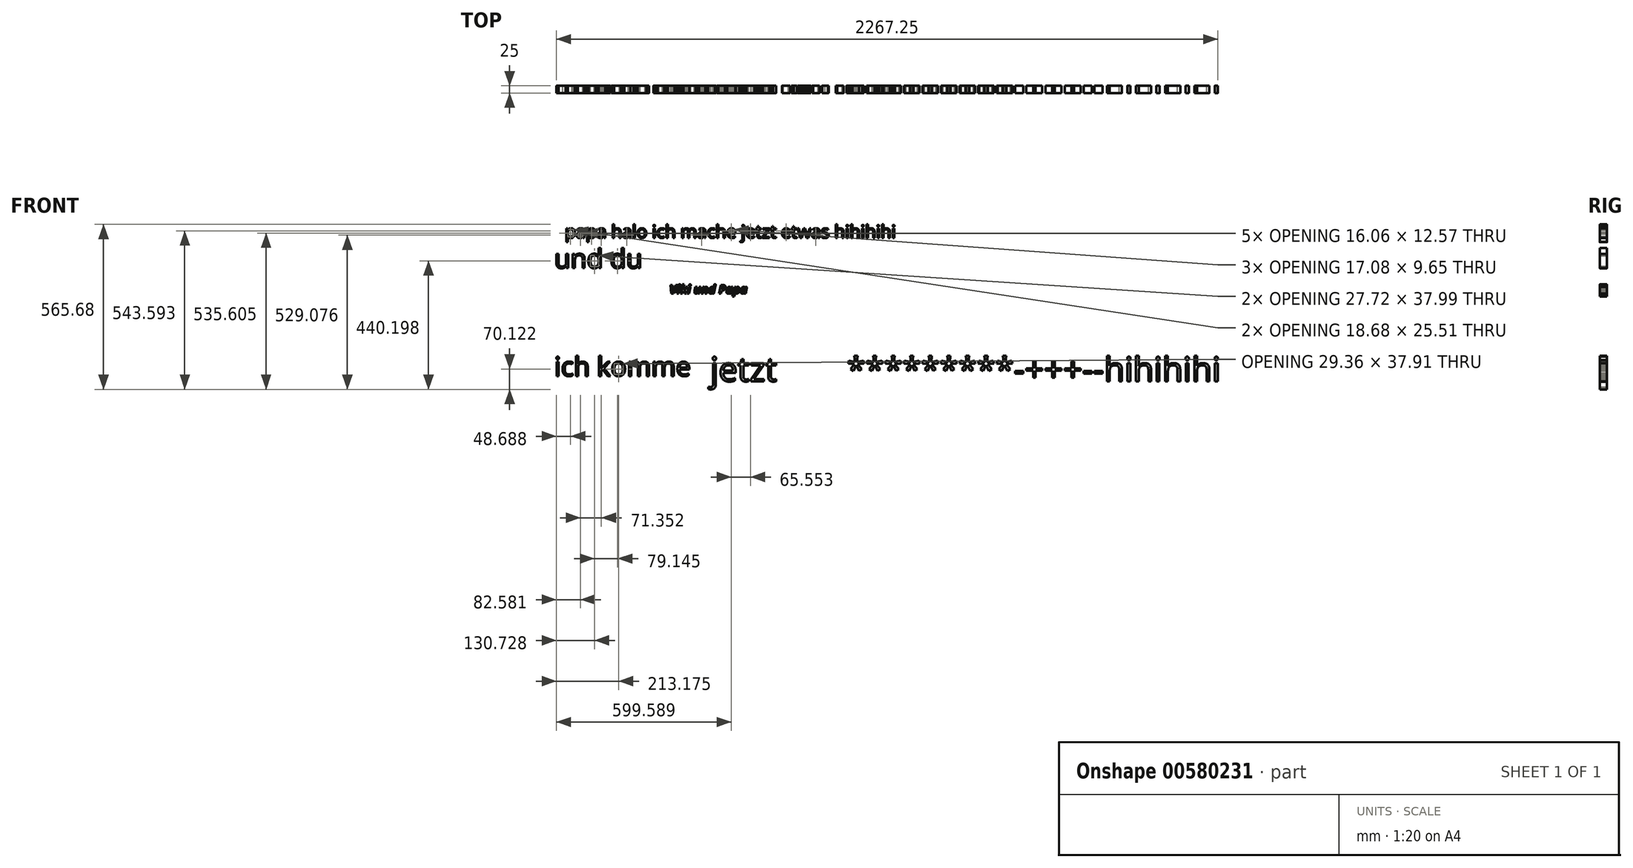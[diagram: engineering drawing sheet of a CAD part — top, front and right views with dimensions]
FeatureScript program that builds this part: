
annotation { "Feature Type Name" : "Feature", "Feature Type Description" : "" }
export const myFeature = defineFeature(function(context is Context, id is Id, definition is map)
    precondition{}
    {
        {
            var Q0;
            Q0=qCreatedBy(makeId("Front.planeOp"),FACE);
            var sketch = newSketch(context, id + "F0", { "sketchPlane" : qUnion([Q0])});
            skText(sketch, "E0", { "text": "papa halo ich mache jetzt etwas hihihihi", "fontName": "OpenSans-Regular.ttf"});
            const initialGuessF0  = {"E0": [-0.0227, 0.032, 1, 0, 0.04395]};
            skSetInitialGuess(sketch, initialGuessF0);
            skSolve(sketch);
        }
        {
            var Q0;
            Q0 = qSketchRegion(id + "F0", true);
            extrude(context, id + "F1", {"entities" : qUnion([Q0]), "depth" : 25 * mm, "offsetDistance" : 25 * mm});
        }
        {
            var Q0;
            Q0=qCreatedBy(makeId("Front.planeOp"),FACE);
            var sketch = newSketch(context, id + "F2", { "sketchPlane" : qUnion([Q0])});
            skText(sketch, "E1", { "text": "und du \n\n\nich komme", "fontName": "OpenSans-Regular.ttf"});
            const initialGuessF2  = {"E1": [-0.05902, -0.07137, 1, 0, 0.0653]};
            skSetInitialGuess(sketch, initialGuessF2);
            skSolve(sketch);
        }
        {
            var Q0;
            Q0 = qSketchRegion(id + "F2", true);
            extrude(context, id + "F3", {"entities" : qUnion([Q0]), "depth" : 25 * mm, "offsetDistance" : 25 * mm});
        }
        {
            var Q0;
            Q0=qCreatedBy(makeId("Front.planeOp"),FACE);
            var sketch = newSketch(context, id + "F4", { "sketchPlane" : qUnion([Q0])});
            skText(sketch, "E2", { "text": "jetzt        *********-+++--hihihihi", "fontName": "OpenSans-Regular.ttf"});
            const initialGuessF4  = {"E2": [0.475, -0.4596, 1, 0, 0.08298]};
            skSetInitialGuess(sketch, initialGuessF4);
            skSolve(sketch);
        }
        {
            var Q0;
            Q0 = qSketchRegion(id + "F4", true);
            extrude(context, id + "F5", {"entities" : qUnion([Q0]), "depth" : 25 * mm, "offsetDistance" : 25 * mm});
        }
        {
            var Q0;
            Q0=qCreatedBy(makeId("Front.planeOp"),FACE);
            var sketch = newSketch(context, id + "F6", { "sketchPlane" : qUnion([Q0])});
            skText(sketch, "E3", { "text": "Viki und Papa", "fontName": "OpenSans-BoldItalic.ttf"});
            const initialGuessF6  = {"E3": [0.33582, -0.15883, 1, 0, 0.0298]};
            skSetInitialGuess(sketch, initialGuessF6);
            skSolve(sketch);
        }
        {
            var Q0;
            Q0 = qSketchRegion(id + "F6", true);
            extrude(context, id + "F7", {"entities" : qUnion([Q0]), "depth" : 25 * mm, "offsetDistance" : 25 * mm});
        }
        {
            var Q0;
            Q0=makeQuery(id+"F7.opExtrude","CAP_EDGE",EDGE,{"disambiguationData":[OSD([sQuery(id+"F6.wireOp",EDGE,"E3.sketch_text.stroke-184")])],"isStart":false});
            fillet(context, id + "F8", {"entities" : qUnion([Q0]), "radius" : 3 * mm, "tangentPropagation" : true, "allowEdgeOverflow" : false});
        }
        {
            var Q0;
            Q0=makeQuery(id+"F7.opExtrude","CAP_FACE",FACE,{"disambiguationData":[OSD([sQuery(id+"F6.wireOp",EDGE,"E3.sketch_text.stroke-82"),sQuery(id+"F6.wireOp",EDGE,"E3.sketch_text.stroke-83"),sQuery(id+"F6.wireOp",EDGE,"E3.sketch_text.stroke-84"),sQuery(id+"F6.wireOp",EDGE,"E3.sketch_text.stroke-85"),sQuery(id+"F6.wireOp",EDGE,"E3.sketch_text.stroke-86"),sQuery(id+"F6.wireOp",EDGE,"E3.sketch_text.stroke-87"),sQuery(id+"F6.wireOp",EDGE,"E3.sketch_text.stroke-88"),sQuery(id+"F6.wireOp",EDGE,"E3.sketch_text.stroke-89"),sQuery(id+"F6.wireOp",EDGE,"E3.sketch_text.stroke-90"),sQuery(id+"F6.wireOp",EDGE,"E3.sketch_text.stroke-91"),sQuery(id+"F6.wireOp",EDGE,"E3.sketch_text.stroke-92"),sQuery(id+"F6.wireOp",EDGE,"E3.sketch_text.stroke-93"),sQuery(id+"F6.wireOp",EDGE,"E3.sketch_text.stroke-94"),sQuery(id+"F6.wireOp",EDGE,"E3.sketch_text.stroke-95"),sQuery(id+"F6.wireOp",EDGE,"E3.sketch_text.stroke-96"),sQuery(id+"F6.wireOp",EDGE,"E3.sketch_text.stroke-97"),sQuery(id+"F6.wireOp",EDGE,"E3.sketch_text.stroke-98"),sQuery(id+"F6.wireOp",EDGE,"E3.sketch_text.stroke-99"),sQuery(id+"F6.wireOp",EDGE,"E3.sketch_text.stroke-100"),sQuery(id+"F6.wireOp",EDGE,"E3.sketch_text.stroke-101"),sQuery(id+"F6.wireOp",EDGE,"E3.sketch_text.stroke-102"),sQuery(id+"F6.wireOp",EDGE,"E3.sketch_text.stroke-103"),sQuery(id+"F6.wireOp",EDGE,"E3.sketch_text.stroke-104"),sQuery(id+"F6.wireOp",EDGE,"E3.sketch_text.stroke-105"),sQuery(id+"F6.wireOp",EDGE,"E3.sketch_text.stroke-106"),sQuery(id+"F6.wireOp",EDGE,"E3.sketch_text.stroke-107"),sQuery(id+"F6.wireOp",EDGE,"E3.sketch_text.stroke-108")])],"isStart":false});
            var Q1;
            Q1=makeQuery(id+"F7.opExtrude","SWEPT_EDGE",EDGE,{"disambiguationData":[OSD([sQuery(id+"F6.wireOp",EDGE,"E3.sketch_text.stroke-93"),sQuery(id+"F6.wireOp",EDGE,"E3.sketch_text.stroke-94")])]});
            var Q2;
            Q2=makeQuery(id+"F7.opExtrude","SWEPT_EDGE",EDGE,{"disambiguationData":[OSD([sQuery(id+"F6.wireOp",EDGE,"E3.sketch_text.stroke-92"),sQuery(id+"F6.wireOp",EDGE,"E3.sketch_text.stroke-93")])]});
            var Q3;
            Q3=makeQuery(id+"F7.opExtrude","SWEPT_EDGE",EDGE,{"disambiguationData":[OSD([sQuery(id+"F6.wireOp",EDGE,"E3.sketch_text.stroke-95"),sQuery(id+"F6.wireOp",EDGE,"E3.sketch_text.stroke-96")])]});
            var Q4;
            Q4=makeQuery(id+"F7.opExtrude","SWEPT_EDGE",EDGE,{"disambiguationData":[OSD([sQuery(id+"F6.wireOp",EDGE,"E3.sketch_text.stroke-94"),sQuery(id+"F6.wireOp",EDGE,"E3.sketch_text.stroke-95")])]});
            fillet(context, id + "F9", {"entities" : qUnion([Q0, Q1, Q2, Q3, Q4]), "radius" : 1 * mm, "tangentPropagation" : true, "allowEdgeOverflow" : false});
        }
        {
            var Q0;
            Q0=makeQuery(id+"F8.opFillet","BLEND_EDGE",EDGE,{"blendedFrom":[makeQuery(id+"F7.opExtrude","CAP_EDGE",EDGE,{"disambiguationData":[OSD([sQuery(id+"F6.wireOp",EDGE,"E3.sketch_text.stroke-184")])],"isStart":false}),makeQuery(id+"F7.opExtrude","SWEPT_FACE",FACE,{"disambiguationData":[OSD([sQuery(id+"F6.wireOp",EDGE,"E3.sketch_text.stroke-183")])]})],"blendedInto":[makeQuery(id+"F7.opExtrude","SWEPT_FACE",FACE,{"disambiguationData":[OSD([sQuery(id+"F6.wireOp",EDGE,"E3.sketch_text.stroke-183")])]})]});
            fillet(context, id + "F10", {"entities" : qUnion([Q0]), "radius" : 2 * mm, "tangentPropagation" : true, "allowEdgeOverflow" : false});
        }
    });
